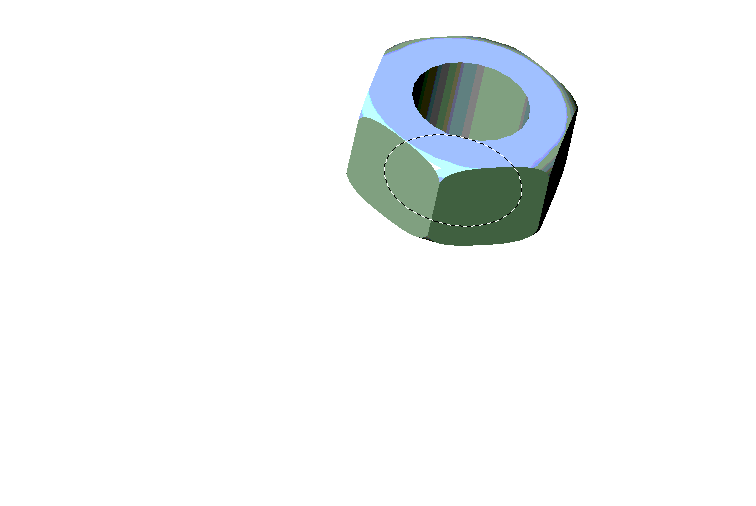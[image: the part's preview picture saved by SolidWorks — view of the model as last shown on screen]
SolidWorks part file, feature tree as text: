
SOLIDWORKS PART (.sldprt)
format: sldprt  version: not decoded by parser v0  size: 154,112 bytes
history: native  units: mm
features: plane x4, sketch x3, material x1, extrude x1, cut_revolve x1, cut_extrude x1, thread x1, mirror x1 + 2 further entries (+7 scaffold rows collapsed)
feature tree (22):
  scaffold x7  (default folders/planes/origin — collapsed)
  material  "Matériau <non spécifié>"
  "Corps de surface"
  plane  "Plane1"
  plane  "Plane2"
  plane  "Plane3"
  "Famille de pièces"
  sketch  "Head Sketch"  dims[D1=60.0deg D2=60.0deg Flats=10.0mm]
  extrude  "Head"  Depth=5.2mm Height=5.2mm
  sketch  "Sketch5"  dims[D1=1.0mm]
  cut_revolve  "Head Trim"  Angle=360deg
  sketch  "Hole Sketch"  dims[Hole Dia=6.0mm]
  cut_extrude  "Through Hole"  [1 undecoded]
  thread  "Cosmetic Thread1"  Diameter=7mm  [1 undecoded]
  plane  "Plan1"  Offset=2.6mm
  mirror  "Symétrie2"
decode coverage: 6 of 8 modeling features carry decoded parameters; 2 rows unclassified (native names shown)
note: 2 parameter values undecoded
note: suppression state not decoded; provenance and decode notes live in map.json
